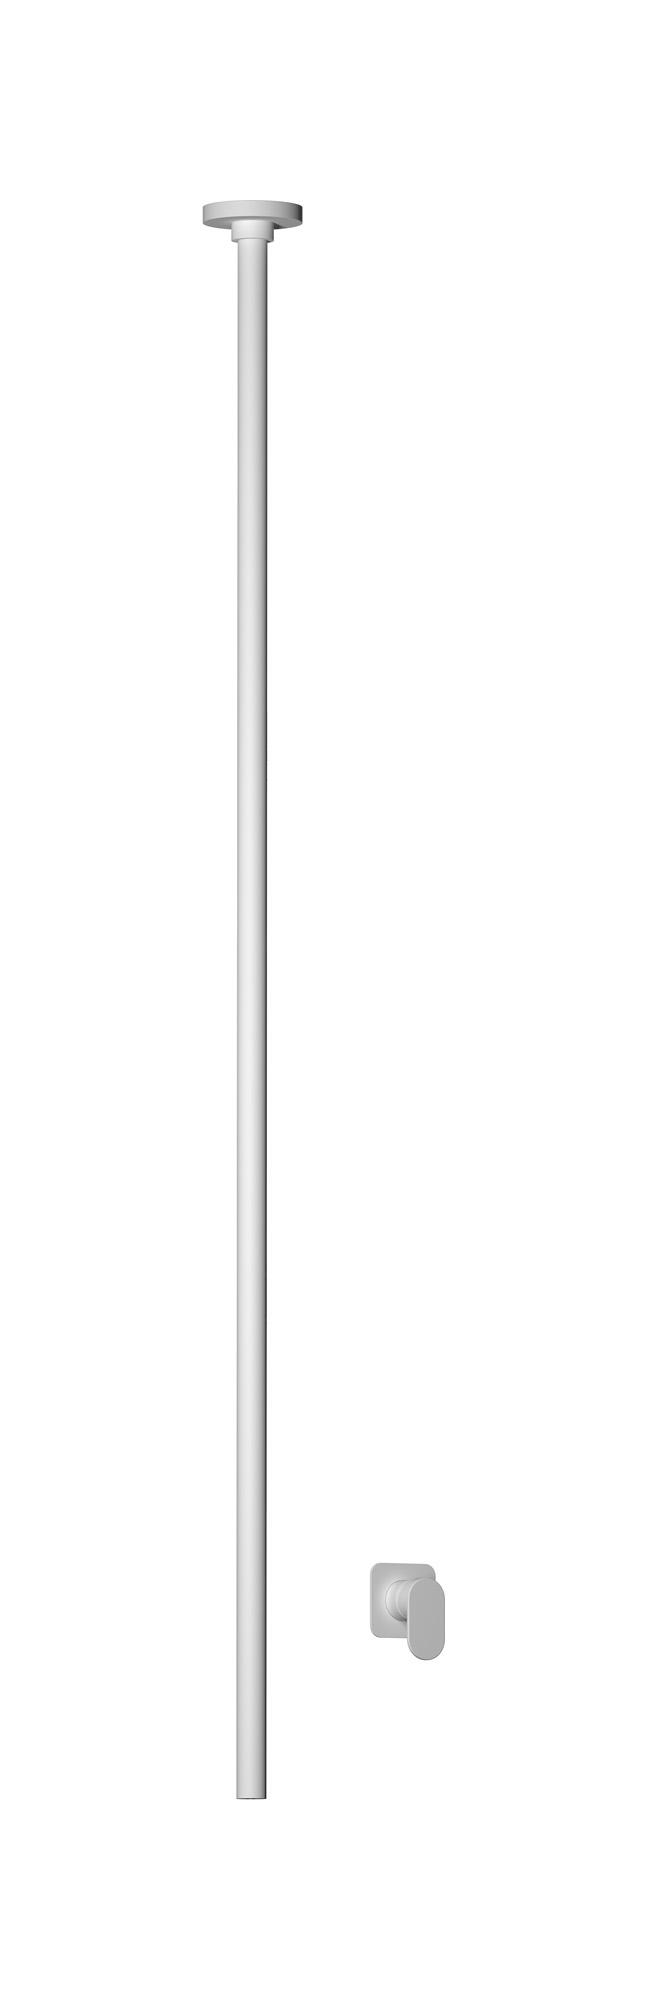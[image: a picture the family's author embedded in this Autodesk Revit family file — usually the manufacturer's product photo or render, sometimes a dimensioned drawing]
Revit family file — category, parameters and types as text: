
# Revit family: K2210
name_source: partatom
category: Apparecchi idraulici
units: mm (PartAtom-declared; Revit-internal decimal feet)

## family parameters
Basato su piano di lavoro = No
Condiviso = No
Mantieni orientamento annotazione = No
Numero OmniClass = 23.45.55.17
Punto di calcolo locali = No
Quota connettore circolare = Usa diametro
Sempre verticale = Sì
Taglio con vuoti quando caricato = No
Tipo di parte = Normale
Titolo OmniClass = Mixing Faucets

## types (4) — shared parameters
Cold water inlet = 10 mm  [stored 0.0328084 ft]
Commenti sul tipo = Wall mixer
Connessione CW = No
Connessione HW = No
Connessione di scarico = No
Connessione di ventilazione = No
Descrizione = Ceiling spout with wall mounted mixer
Hot water inlet = 10 mm  [stored 0.0328084 ft]
Produttore = IB Rubinetterie S.p.A.
URL = https://www.weareib.it
zero-valued in all types: Prospetto di default

## per-type parameters (varying)
| type | Finishes surface | Immagine tipo | Modello |
| Chrome | IB_Chrome | K2210CC.jpg | K2210CC |
| Brushed nickel | IB_Brushed nickel | K2210SS.jpg | K2210SS |
| Matt white | IB_matt white | K2210BO.jpg | K2210BO |
| Matt black | IB_matt black | K2210NP.jpg | K2210NP |

note: [stored X ft] marks values corroborated as IEEE doubles in the binary element streams (Revit-internal decimal feet)
